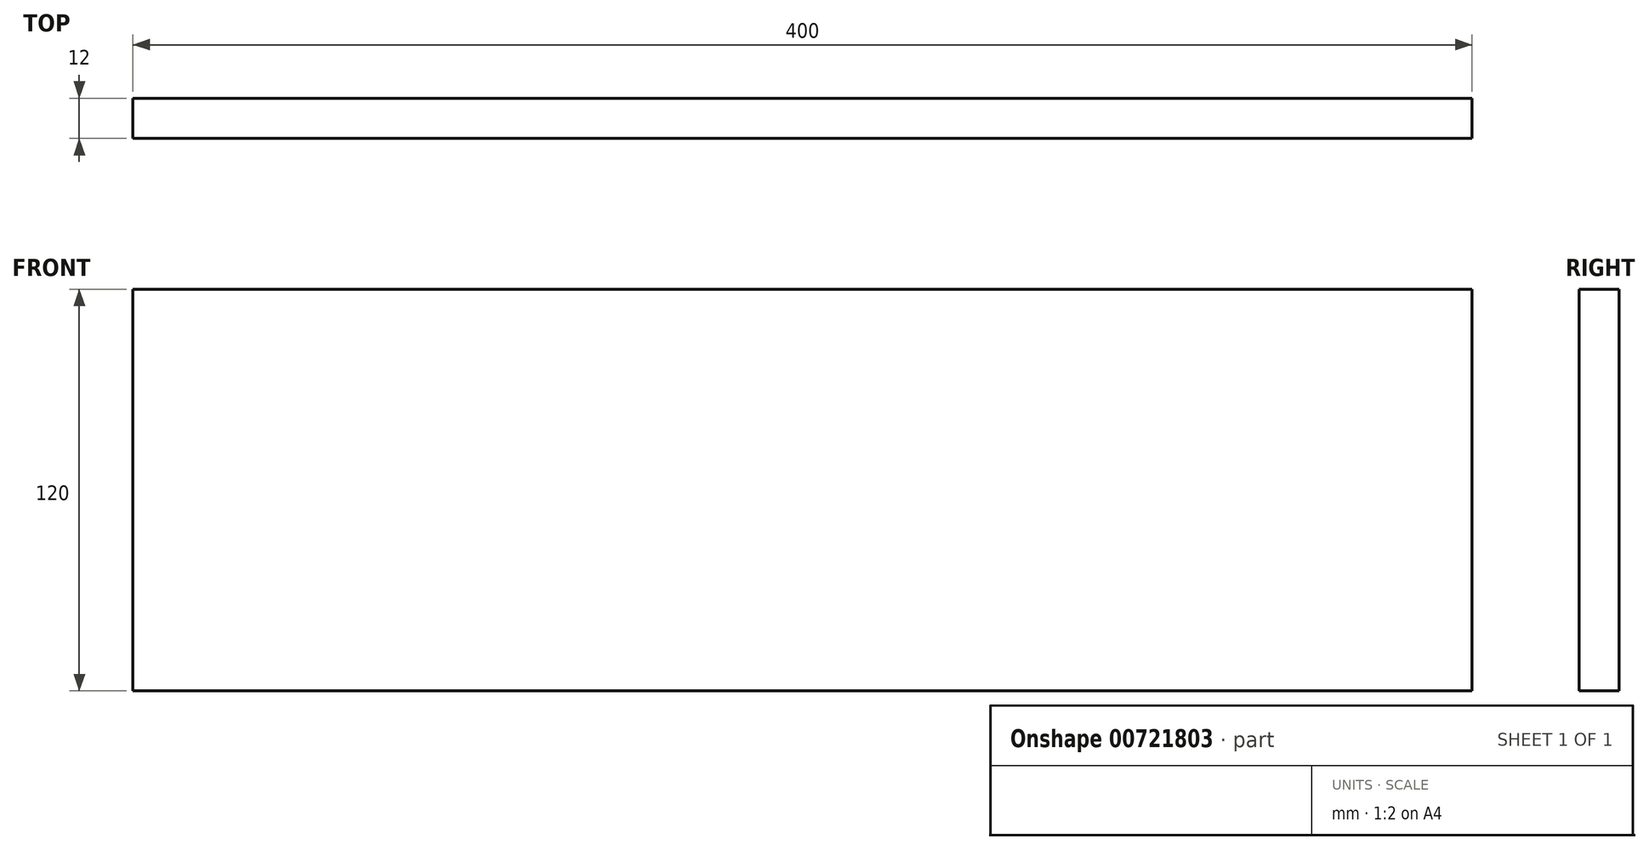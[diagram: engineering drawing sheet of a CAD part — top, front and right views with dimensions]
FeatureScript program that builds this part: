
annotation { "Feature Type Name" : "Feature", "Feature Type Description" : "" }
export const myFeature = defineFeature(function(context is Context, id is Id, definition is map)
    precondition{}
    {
        {
            var Q0;
            Q0=qCreatedBy(makeId("Front.planeOp"),FACE);
            var sketch = newSketch(context, id + "F0", { "sketchPlane" : qUnion([Q0])});
            skLineSegment(sketch, "E0.bottom", {"start": v(200, -60) * mm, "end": v(-200, -60) * mm});
            skLineSegment(sketch, "E0.top", {"start": v(200, 60) * mm, "end": v(-200, 60) * mm});
            skLineSegment(sketch, "E0.left", {"start": v(200, -60) * mm, "end": v(200, 60) * mm});
            skLineSegment(sketch, "E0.right", {"start": v(-200, -60) * mm, "end": v(-200, 60) * mm});
            skPoint(sketch, "E0.middle", {"position": v(0, 0) * mm});
            skSolve(sketch);
        }
        {
            var Q0;
            Q0 = qSketchRegion(id + "F0", true);
            extrude(context, id + "F1", {"entities" : qUnion([Q0]), "depth" : 12 * mm, "offsetDistance" : 25 * mm});
        }
    });
